# Revit family: EC5-TY3232_Metric
name_source: partatom
category: Sprinklers
units: mm (PartAtom-declared; Revit-internal decimal feet)

## family parameters
Always vertical = Yes
Cut with Voids When Loaded = No
Maintain Annotation Orientation = No
OmniClass Number = 23.65.70.17.11.24
OmniClass Title = Fire Fighting Sprinkler Heads
Part Type = Normal
Room Calculation Point = No
Round Connector Dimension = Use Diameter
Shared = No
Work Plane-Based = No

## types (6) — shared parameters
COBie = Yes
COBie.Type = Yes
COBie.Type.AssetType = Fixed
COBie.Type.Category = Pr_70_55_97_84:Sprinklers
COBie.Type.DurationUnit = year
COBie.Type.Manufacturer = Tyco Fire Protection Products
COBie.Type.Material = Bronze
COBie.Type.Shape = Cylinder
COBie.Type.Size = 1/2"(DN15)
COBie.Type.WarrantyGuarantorParts = http://tycofsbp.com
Coverage = Extended
Coverage_ = Extended
K-Factor = 79.9096
Manufacturer = Tyco Fire Protection Products
Manufacturer URL = www.tyco-fire.com
Material_ = Bronze
Model = EC-5
Nominal Diameter 1 = 15 mm
Orifice = Standard
Orifice Size = 11 mm
Outside Diameter 1 = 21 mm
Response = Quick
Response_ = Quick
SIN No = TY3232
Takeout 1 = 52 mm
Technical Data Sheet No = TFP228
zero-valued in all types: COBie.Type.NominalHeight, COBie.Type.NominalLength, COBie.Type.NominalWidth, COBie.Type.ReplacementCost, Default Elevation, Style Id

## per-type parameters (varying)
| type | COBie.Component.Description | COBie.Component.Name | COBie.Type.Colour | COBie.Type.Finish | COBie.Type.ModelNumber | COBie.Type.ModelReference | Description | Finish_ | Part No | Temperature Rating |
| EC-5, Recessed Pendent Sprinklers 1/2" NPT K=5.6 57°C Brass_51-051-1-135 | EC-5 Wet Pendent  57.2°C K80 DN15 NPT Br | Sprinklers:Pendent_135 | Yellow | Natural Brass | 51-051-1-135 | EC-5 Wet Pendent  57.2°C K80 DN15 NPT Br | EC-5, Recessed Pendent Sprinklers 1/2" NPT K=5.6 57°C Brass | Natural Brass | 51-051-1-135 | 57 °C |
| EC-5, Recessed Pendent Sprinklers 1/2" NPT K=5.6 68°C Brass_51-051-1-155 | EC-5 Wet Pendent  68.3°C K80 DN15 NPT Br | Sprinklers:Pendent_155 | Yellow | Natural Brass | 51-051-1-155 | EC-5 Wet Pendent  68.3°C K80 DN15 NPT Br | EC-5, Recessed Pendent Sprinklers 1/2" NPT K=5.6 68°C Brass | Natural Brass | 51-051-1-155 | 68 °C |
| EC-5, Recessed Pendent Sprinklers 1/2" NPT K=5.6 57°C White_51-051-4-135 | EC-5 Wet Pendent  57.2°C K80 DN15 NPT Wh9003 | Sprinklers:Pendent_135 | White | Signal White | 51-051-4-135 | EC-5 Wet Pendent  57.2°C K80 DN15 NPT Wh9003 | EC-5, Recessed Pendent Sprinklers 1/2" NPT K=5.6 57°C White | White RAL9003 | 51-051-4-135 | 57 °C |
| EC-5, Recessed Pendent Sprinklers 1/2" NPT K=5.6 68°C White_51-051-4-155 | EC-5 Wet Pendent  68.3°C K80 DN15 NPT Wh9003 | Sprinklers:Pendent_155 | White | Signal White | 51-051-4-155 | EC-5 Wet Pendent  68.3°C K80 DN15 NPT Wh9003 | EC-5, Recessed Pendent Sprinklers 1/2" NPT K=5.6 68°C White | White RAL9003 | 51-051-4-155 | 68 °C |
| EC-5, Recessed Pendent Sprinklers 1/2" NPT K=5.6 57°C Chrome_51-051-9-135 | EC-5 Wet Pendent  57.2°C K80 DN15 NPT Chr | Sprinklers:Pendent_135 | Silver | Chrome Plated | 51-051-9-135 | EC-5 Wet Pendent  57.2°C K80 DN15 NPT Chr | EC-5, Recessed Pendent Sprinklers 1/2" NPT K=5.6 57°C Chrome | Chrome Plated | 51-051-9-135 | 57 °C |
| EC-5, Recessed Pendent Sprinklers 1/2" NPT K=5.6 68°C Chrome_51-051-9-155 | EC-5 Wet Pendent  68.3°C K80 DN15 NPT Chr | Sprinklers:Pendent_155 | Silver | Chrome Plated | 51-051-9-155 | EC-5 Wet Pendent  68.3°C K80 DN15 NPT Chr | EC-5, Recessed Pendent Sprinklers 1/2" NPT K=5.6 68°C Chrome | Chrome Plated | 51-051-9-155 | 68 °C |

## geometry (parser evidence)
native form markers: Blend x2, Sweep x46
no freeform markers — native parametric forms only
